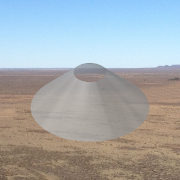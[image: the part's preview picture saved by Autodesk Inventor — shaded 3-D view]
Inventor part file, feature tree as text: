
AUTODESK INVENTOR PART (.ipt)
format: ipt  version: 2013 SP2 (Build 170200200, 200)  size: 156,160 bytes
history: native  units: in
note: dims shown in document units (in); Inventor stores cm internally (conversion verified against a paired STEP export)
features: sketch x2, revolve x1, plane x1, extrude x1
ambient origin geometry x8: Origin, YZ Plane, XZ Plane, XY Plane, X Axis, Y Axis, Z Axis, Center Point
bodies: Solid1 (feature_tree)
feature tree (5):
  revolve  "Revolution1"  Angle=45.0deg
  plane  "Work Plane1"
  extrude  "Extrusion2"  Depth=20.0in
  sketch  "Sketch1"  dims[d0=-0.0in d1=45.0deg]
  sketch  "Sketch5"  dims[d2=90.0deg d3=20.0in d7=10.0in d9=20.0in d10=0.0in]
